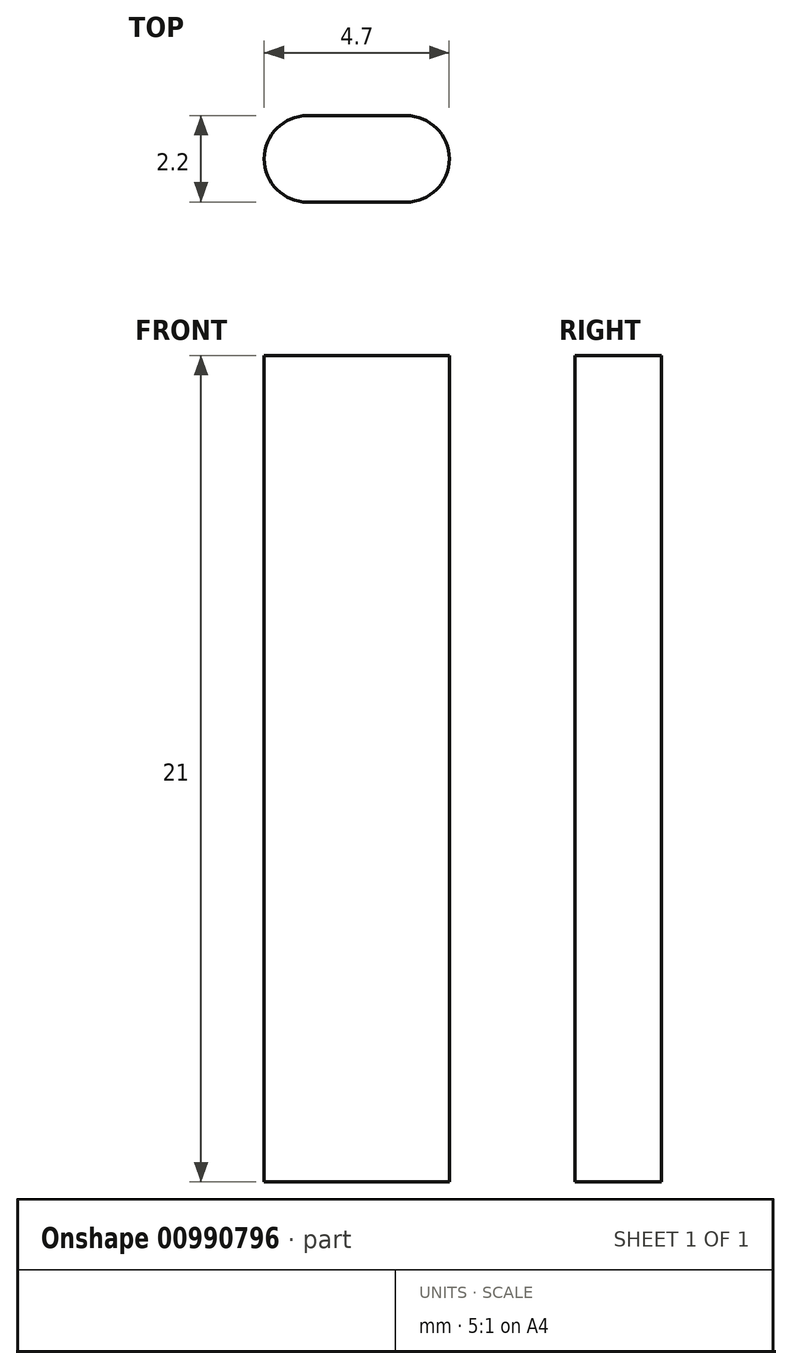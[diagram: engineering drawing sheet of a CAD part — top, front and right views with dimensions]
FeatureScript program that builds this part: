
annotation { "Feature Type Name" : "Feature", "Feature Type Description" : "" }
export const myFeature = defineFeature(function(context is Context, id is Id, definition is map)
    precondition{}
    {
        {
            var Q0;
            Q0=qCreatedBy(makeId("Top.planeOp"),FACE);
            var sketch = newSketch(context, id + "F0", { "sketchPlane" : qUnion([Q0])});
            skPoint(sketch, "E0", {"position": v(16.27, 12.24) * mm});
            skArc(sketch, "E1", {"start": v(16.27, 13.34) * mm, "mid": v(17.37, 12.24) * mm, "end": v(16.27, 11.14) * mm});
            skLineSegment(sketch, "E2", {"start": v(16.27, 13.34) * mm, "end": v(13.77, 13.34) * mm});
            skLineSegment(sketch, "E3", {"start": v(16.27, 11.14) * mm, "end": v(13.77, 11.14) * mm});
            skArc(sketch, "E4", {"start": v(13.77, 13.34) * mm, "mid": v(12.67, 12.24) * mm, "end": v(13.77, 11.14) * mm});
            skPoint(sketch, "E5", {"position": v(16.27, 6.64) * mm});
            skArc(sketch, "E6", {"start": v(16.27, 7.74) * mm, "mid": v(17.37, 6.64) * mm, "end": v(16.27, 5.54) * mm});
            skLineSegment(sketch, "E7", {"start": v(16.27, 7.74) * mm, "end": v(13.77, 7.74) * mm});
            skLineSegment(sketch, "E8", {"start": v(16.27, 5.54) * mm, "end": v(13.77, 5.54) * mm});
            skArc(sketch, "E9", {"start": v(13.77, 7.74) * mm, "mid": v(12.67, 6.64) * mm, "end": v(13.77, 5.54) * mm});
            skLineSegment(sketch, "E10.1.0.0", {"start": v(9.87, 5.54) * mm, "end": v(7.37, 5.54) * mm});
            skArc(sketch, "E10.1.0.1", {"start": v(9.87, 7.74) * mm, "mid": v(10.97, 6.64) * mm, "end": v(9.87, 5.54) * mm});
            skArc(sketch, "E10.1.0.2", {"start": v(7.37, 7.74) * mm, "mid": v(6.27, 6.64) * mm, "end": v(7.37, 5.54) * mm});
            skArc(sketch, "E10.1.0.3", {"start": v(7.37, 13.44) * mm, "mid": v(6.27, 12.34) * mm, "end": v(7.37, 11.24) * mm});
            skLineSegment(sketch, "E10.1.0.4", {"start": v(9.87, 11.24) * mm, "end": v(7.37, 11.24) * mm});
            skLineSegment(sketch, "E10.1.0.5", {"start": v(9.87, 13.44) * mm, "end": v(7.37, 13.44) * mm});
            skPoint(sketch, "E10.1.0.6", {"position": v(9.87, 12.34) * mm});
            skArc(sketch, "E10.1.0.7", {"start": v(9.87, 13.44) * mm, "mid": v(10.97, 12.34) * mm, "end": v(9.87, 11.24) * mm});
            skPoint(sketch, "E10.1.0.8", {"position": v(9.87, 6.64) * mm});
            skLineSegment(sketch, "E10.1.0.9", {"start": v(9.87, 7.74) * mm, "end": v(7.37, 7.74) * mm});
            skArc(sketch, "E11.0.1.0", {"start": v(16.27, 2.14) * mm, "mid": v(17.37, 1.04) * mm, "end": v(16.27, -0.06) * mm});
            skPoint(sketch, "E11.0.1.1", {"position": v(16.27, 1.04) * mm});
            skArc(sketch, "E11.0.1.2", {"start": v(16.27, -3.46) * mm, "mid": v(17.37, -4.56) * mm, "end": v(16.27, -5.66) * mm});
            skLineSegment(sketch, "E11.0.1.3", {"start": v(16.27, -3.46) * mm, "end": v(13.77, -3.46) * mm});
            skLineSegment(sketch, "E11.0.1.4", {"start": v(16.27, -5.66) * mm, "end": v(13.77, -5.66) * mm});
            skArc(sketch, "E11.0.1.5", {"start": v(13.77, -3.46) * mm, "mid": v(12.67, -4.56) * mm, "end": v(13.77, -5.66) * mm});
            skPoint(sketch, "E11.0.1.6", {"position": v(16.27, -4.56) * mm});
            skLineSegment(sketch, "E11.0.1.7", {"start": v(16.27, -0.06) * mm, "end": v(13.77, -0.06) * mm});
            skLineSegment(sketch, "E11.0.1.8", {"start": v(16.27, 2.14) * mm, "end": v(13.77, 2.14) * mm});
            skArc(sketch, "E11.0.1.9", {"start": v(13.77, 2.14) * mm, "mid": v(12.67, 1.04) * mm, "end": v(13.77, -0.06) * mm});
            skLineSegment(sketch, "E11.direction2", {"start": v(13.77, 5.54) * mm, "end": v(13.77, -5.66) * mm, "construction": true});
            skLineSegment(sketch, "E12", {"start": v(18.27, 12.24) * mm, "end": v(18.27, -4.56) * mm});
            skLineSegment(sketch, "E13", {"start": v(16.27, -6.56) * mm, "end": v(13.77, -6.56) * mm});
            skLineSegment(sketch, "E14", {"start": v(11.77, -4.56) * mm, "end": v(11.77, 4.64) * mm});
            skLineSegment(sketch, "E15", {"start": v(11.77, 4.64) * mm, "end": v(7.37, 4.64) * mm});
            skLineSegment(sketch, "E16", {"start": v(5.37, 6.64) * mm, "end": v(5.37, 12.24) * mm});
            skLineSegment(sketch, "E17", {"start": v(7.37, 14.24) * mm, "end": v(16.27, 14.24) * mm});
            skPoint(sketch, "E18.visualSharp", {"position": v(18.27, 14.24) * mm});
            skArc(sketch, "E18.filletArc", {"start": v(18.27, 12.24) * mm, "mid": v(17.69, 13.65) * mm, "end": v(16.27, 14.24) * mm});
            skPoint(sketch, "E19.visualSharp", {"position": v(5.37, 14.24) * mm});
            skArc(sketch, "E19.filletArc", {"start": v(7.37, 14.24) * mm, "mid": v(5.96, 13.65) * mm, "end": v(5.37, 12.24) * mm});
            skPoint(sketch, "E20.visualSharp", {"position": v(5.37, 4.64) * mm});
            skArc(sketch, "E20.filletArc", {"start": v(5.37, 6.64) * mm, "mid": v(5.96, 5.22) * mm, "end": v(7.37, 4.64) * mm});
            skPoint(sketch, "E21.visualSharp", {"position": v(11.77, -6.56) * mm});
            skArc(sketch, "E21.filletArc", {"start": v(11.77, -4.56) * mm, "mid": v(12.36, -5.98) * mm, "end": v(13.77, -6.56) * mm});
            skPoint(sketch, "E22.visualSharp", {"position": v(18.27, -6.56) * mm});
            skArc(sketch, "E22.filletArc", {"start": v(16.27, -6.56) * mm, "mid": v(17.69, -5.98) * mm, "end": v(18.27, -4.56) * mm});
            skSolve(sketch);
        }
        {
            var Q0;
            Q0=makeQuery(id+"F0.imprint","IMPRINT",FACE,{"disambiguationData":[TD([[makeQuery(id+"F0.imprint","IMPRINT",EDGE,{"derivedFrom":sQuery(id+"F0.wireOp",EDGE,"E1")}),1.0]])]});
            extrude(context, id + "F1", {"entities" : qUnion([Q0]), "depth" : 21 * mm, "offsetDistance" : 25 * mm});
        }
    });
